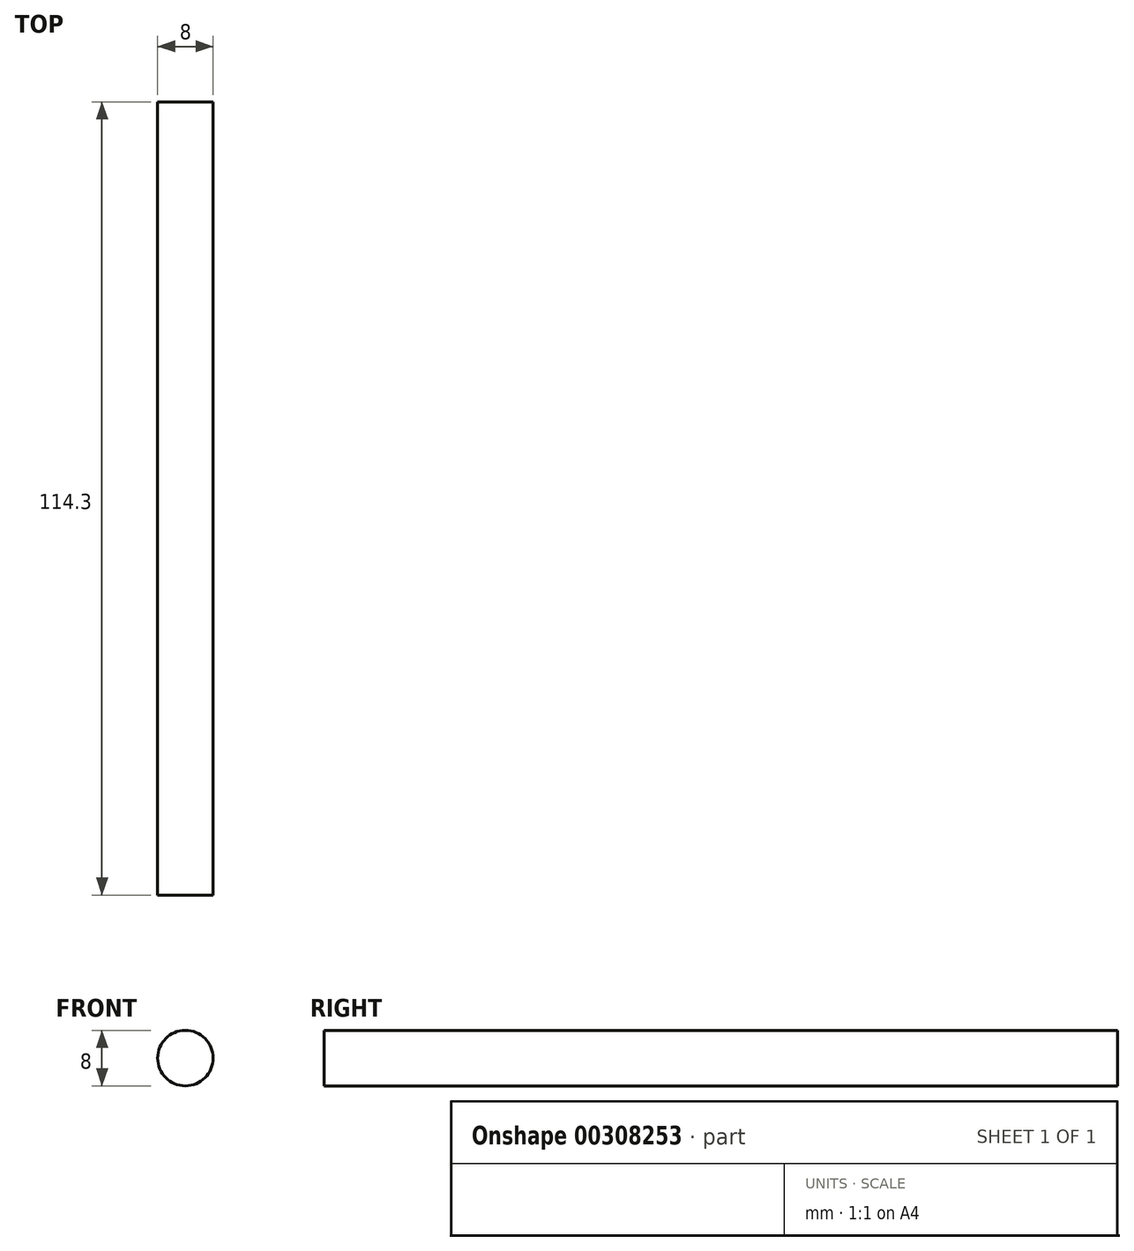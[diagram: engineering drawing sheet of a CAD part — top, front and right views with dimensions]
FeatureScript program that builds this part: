
annotation { "Feature Type Name" : "Feature", "Feature Type Description" : "" }
export const myFeature = defineFeature(function(context is Context, id is Id, definition is map)
    precondition{}
    {
        {
            var Q0;
            Q0=qCreatedBy(makeId("Front.planeOp"),FACE);
            var sketch = newSketch(context, id + "F0", { "sketchPlane" : qUnion([Q0])});
            skCircle(sketch, "E0", {"center": v(0, 0) * mm, "radius": 4 * mm});
            skSolve(sketch);
        }
        {
            var Q0;
            Q0=makeQuery(id+"F0.imprint","IMPRINT",FACE,{"disambiguationData":[TD([[makeQuery(id+"F0.imprint","IMPRINT",EDGE,{"derivedFrom":sQuery(id+"F0.wireOp",EDGE,"E0")}),1.0]])]});
            extrude(context, id + "F1", {"entities" : qUnion([Q0]), "depth" : 114.3 * mm});
        }
    });
